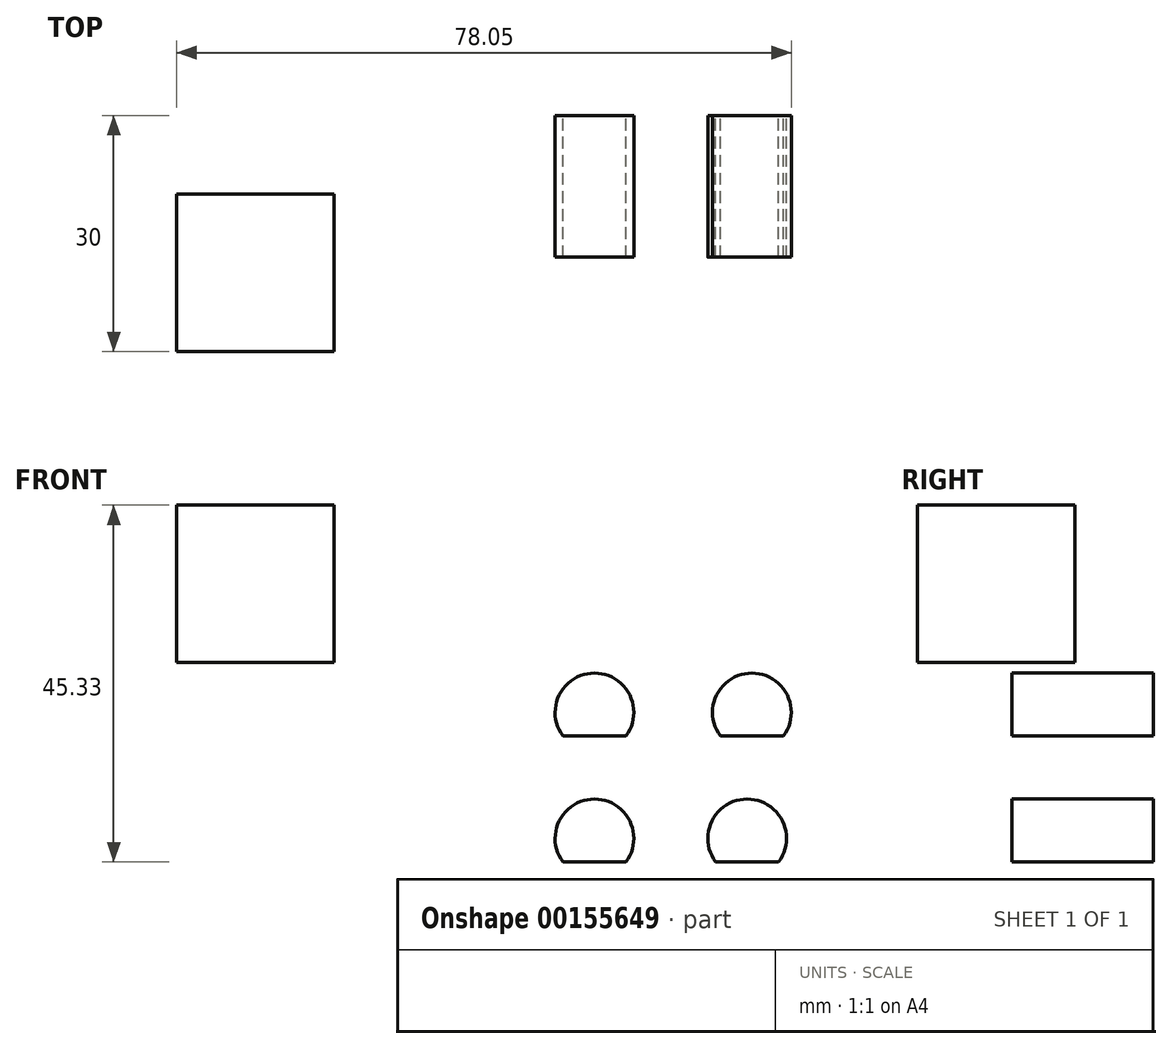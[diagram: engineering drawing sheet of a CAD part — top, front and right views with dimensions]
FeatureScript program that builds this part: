
annotation { "Feature Type Name" : "Feature", "Feature Type Description" : "" }
export const myFeature = defineFeature(function(context is Context, id is Id, definition is map)
    precondition{}
    {
        {
            var Q0;
            Q0=qCreatedBy(makeId("Front.planeOp"),FACE);
            var sketch = newSketch(context, id + "F0", { "sketchPlane" : qUnion([Q0])});
            skCircle(sketch, "E0", {"center": v(0, 0) * mm, "radius": 5 * mm});
            skLineSegment(sketch, "E1", {"start": v(-4, -3) * mm, "end": v(4, -3) * mm});
            skSolve(sketch);
        }
        {
            var Q0;
            {var subQ0=sQuery(id+"F0.wireOp",EDGE,"E1");Q0=makeQuery(id+"F0.imprint","IMPRINT",FACE,{"disambiguationData":[TD([[makeQuery(id+"F0.imprint","IMPRINT",EDGE,{"derivedFrom":subQ0}),1.0]])]});}
            extrude(context, id + "F1", {"entities" : qUnion([Q0]), "depth" : 8 * mm, "hasSecondDirection" : true, "secondDirectionOppositeDirection" : true, "secondDirectionDepth" : 10 * mm});
        }
        {
            var Q0;
            Q0=makeQuery(id+"F1.opExtrude","SWEPT_BODY",BODY,{"disambiguationData":[OSD([sQuery(id+"F0.wireOp",EDGE,"E0"),sQuery(id+"F0.wireOp",EDGE,"E1")])]});
            transform(context, id + "F2", {"entities" : qUnion([Q0]), "transformType" : TransformType.TRANSLATION_3D, "dx" : 0 * mm, "dy" : 0 * mm, "dz" : 16 * mm, "makeCopy" : true});
        }
        {
            var Q0;
            Q0=makeQuery(id+"F1.opExtrude","SWEPT_BODY",BODY,{"disambiguationData":[OSD([sQuery(id+"F0.wireOp",EDGE,"E0"),sQuery(id+"F0.wireOp",EDGE,"E1")])]});
            transform(context, id + "F3", {"entities" : qUnion([Q0]), "transformType" : TransformType.TRANSLATION_3D, "dx" : 19.4 * mm, "dy" : 0 * mm, "dz" : 0 * mm, "makeCopy" : true});
        }
        {
            var Q0;
            Q0=makeQuery(id+"F2.opPattern","COPY",BODY,{"derivedFrom":makeQuery(id+"F1.opExtrude","SWEPT_BODY",BODY,{"disambiguationData":[OSD([sQuery(id+"F0.wireOp",EDGE,"E0"),sQuery(id+"F0.wireOp",EDGE,"E1")])]}),"instanceName":"1"});
            transform(context, id + "F4", {"entities" : qUnion([Q0]), "transformType" : TransformType.TRANSLATION_3D, "dx" : 20 * mm, "dy" : 0 * mm, "dz" : 0 * mm, "makeCopy" : true});
        }
        {
            var Q0;
            Q0=qCreatedBy(makeId("Front.planeOp"),FACE);
            var sketch = newSketch(context, id + "F5", { "sketchPlane" : qUnion([Q0])});
            skLineSegment(sketch, "E2.bottom", {"start": v(-53.05, 42.33) * mm, "end": v(-33.05, 42.33) * mm});
            skLineSegment(sketch, "E2.top", {"start": v(-53.05, 22.33) * mm, "end": v(-33.05, 22.33) * mm});
            skLineSegment(sketch, "E2.left", {"start": v(-53.05, 42.33) * mm, "end": v(-53.05, 22.33) * mm});
            skLineSegment(sketch, "E2.right", {"start": v(-33.05, 42.33) * mm, "end": v(-33.05, 22.33) * mm});
            skSolve(sketch);
        }
        {
            var Q0;
            Q0 = qSketchRegion(id + "F5", true);
            extrude(context, id + "F6", {"entities" : qUnion([Q0]), "depth" : 20 * mm});
        }
    });
